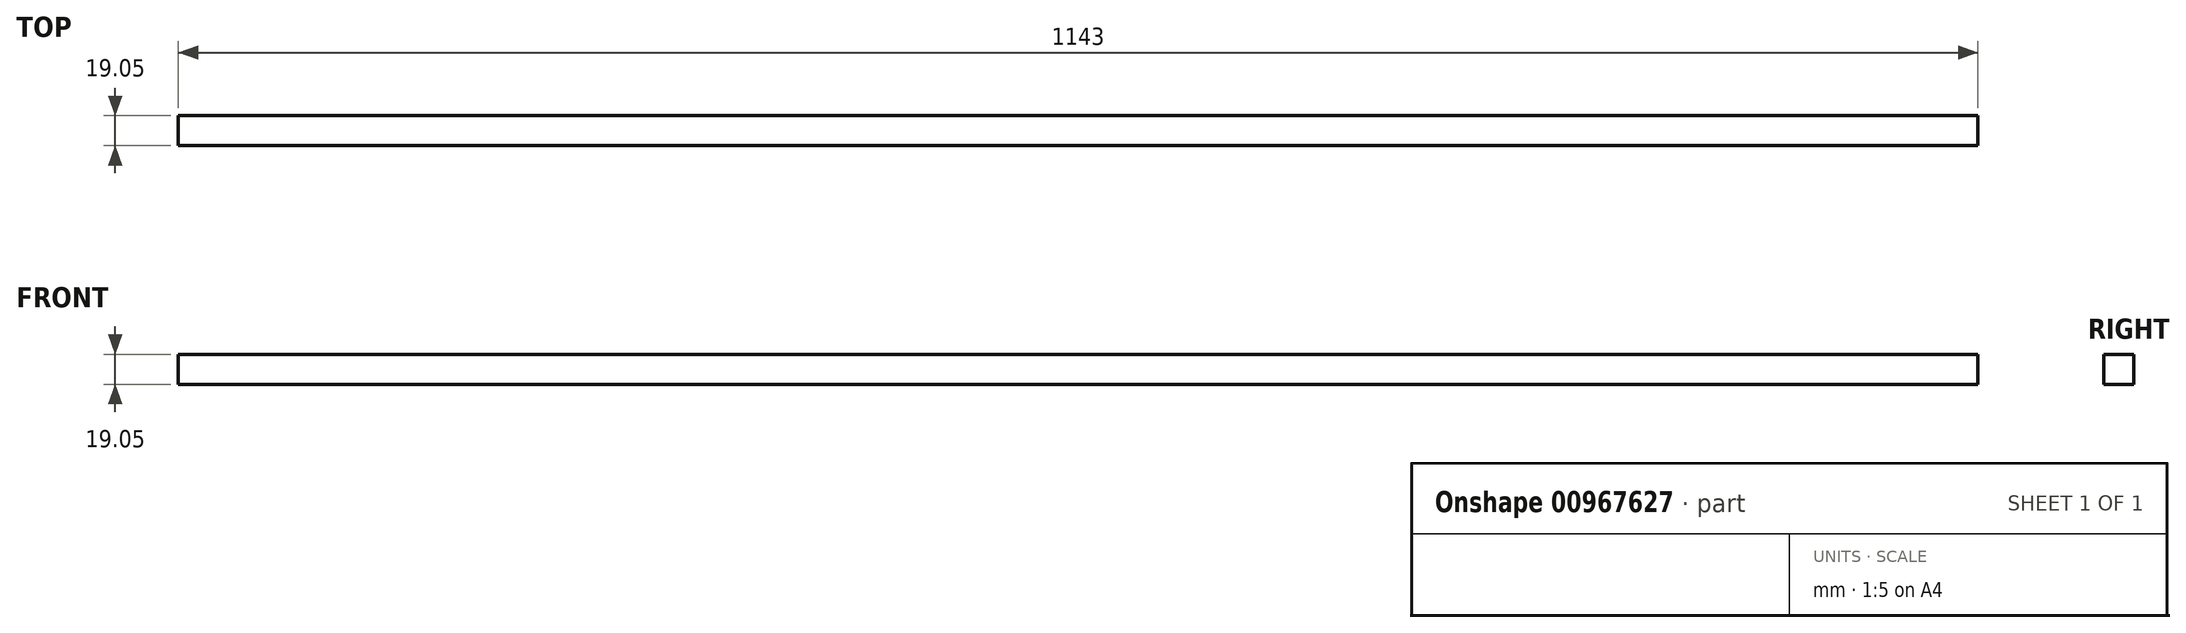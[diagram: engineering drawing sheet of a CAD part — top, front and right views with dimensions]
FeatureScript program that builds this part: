
annotation { "Feature Type Name" : "Feature", "Feature Type Description" : "" }
export const myFeature = defineFeature(function(context is Context, id is Id, definition is map)
    precondition{}
    {
        {
            var Q0;
            Q0=qCreatedBy(makeId("Front.planeOp"),FACE);
            var sketch = newSketch(context, id + "F0", { "sketchPlane" : qUnion([Q0])});
            skLineSegment(sketch, "E0.bottom", {"start": v(0, 0) * mm, "end": v(1143, 0) * mm});
            skLineSegment(sketch, "E0.top", {"start": v(0, 19.05) * mm, "end": v(1143, 19.05) * mm});
            skLineSegment(sketch, "E0.left", {"start": v(0, 0) * mm, "end": v(0, 19.05) * mm});
            skLineSegment(sketch, "E0.right", {"start": v(1143, 0) * mm, "end": v(1143, 19.05) * mm});
            skSolve(sketch);
        }
        {
            var Q0;
            Q0 = qSketchRegion(id + "F0", true);
            extrude(context, id + "F1", {"entities" : qUnion([Q0]), "depth" : 19.05 * mm, "offsetDistance" : 25.4 * mm});
        }
    });
